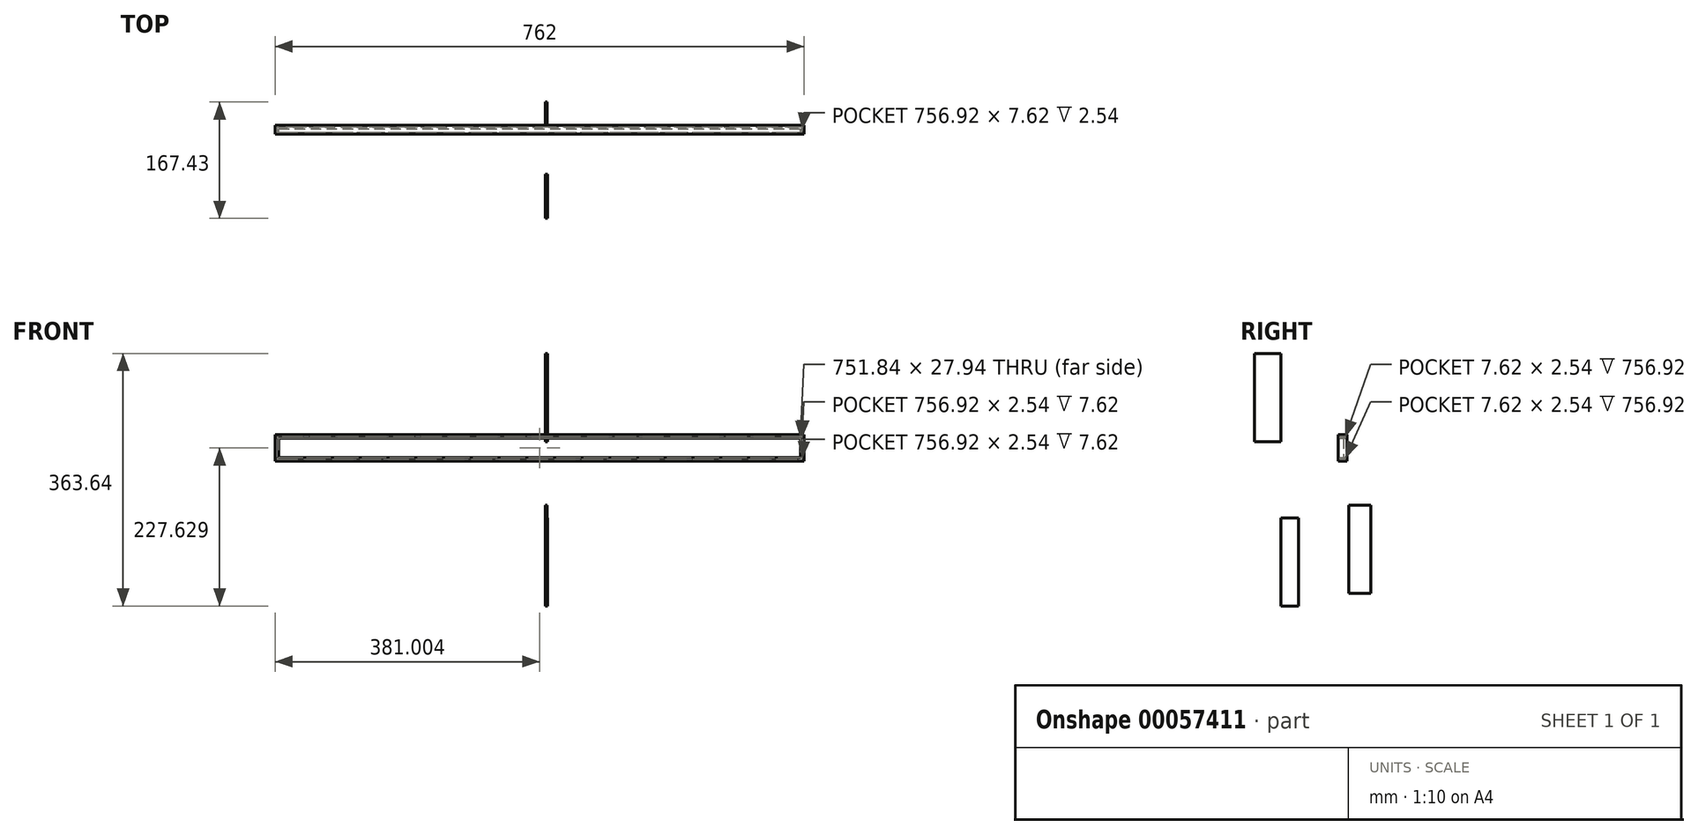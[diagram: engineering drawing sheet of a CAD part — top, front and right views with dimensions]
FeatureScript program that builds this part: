
annotation { "Feature Type Name" : "Feature", "Feature Type Description" : "" }
export const myFeature = defineFeature(function(context is Context, id is Id, definition is map)
    precondition{}
    {
        {
            var Q0;
            Q0=qCreatedBy(makeId("Front.planeOp"),FACE);
            var sketch = newSketch(context, id + "F0", { "sketchPlane" : qUnion([Q0])});
            skLineSegment(sketch, "E0.bottom", {"start": v(-388.9, 51.3) * mm, "end": v(373.1, 51.3) * mm});
            skLineSegment(sketch, "E0.top", {"start": v(-388.9, 13.2) * mm, "end": v(373.1, 13.2) * mm});
            skLineSegment(sketch, "E0.left", {"start": v(-388.9, 51.3) * mm, "end": v(-388.9, 13.2) * mm});
            skLineSegment(sketch, "E0.right", {"start": v(373.1, 51.3) * mm, "end": v(373.1, 13.2) * mm});
            skSolve(sketch);
        }
        {
            var Q0;
            Q0=makeQuery(id+"F0.imprint","IMPRINT",FACE,{"disambiguationData":[TD([[makeQuery(id+"F0.imprint","IMPRINT",EDGE,{"derivedFrom":sQuery(id+"F0.wireOp",EDGE,"E0.bottom")}),-1.0]])]});
            extrude(context, id + "F1", {"entities" : qUnion([Q0]), "depth" : 12.7 * mm});
        }
        {
            var Q0;
            Q0=makeQuery(id+"F1.opExtrude","CAP_FACE",FACE,{"disambiguationData":[OSD([sQuery(id+"F0.wireOp",EDGE,"E0.bottom"),sQuery(id+"F0.wireOp",EDGE,"E0.top"),sQuery(id+"F0.wireOp",EDGE,"E0.left"),sQuery(id+"F0.wireOp",EDGE,"E0.right")])],"isStart":false});
            shell(context, id + "F2", {"entities" : qUnion([Q0]), "thickness" : 5.08 * mm});
        }
        {
            var Q0;
            Q0=makeQuery(id+"F2.opShell","OFFSET_FACE",FACE,{"disambiguationData":[OSD([sQuery(id+"F0.wireOp",EDGE,"E0.bottom")])]});
            var Q1;
            Q1=makeQuery(id+"F2.opShell","OFFSET_FACE",FACE,{"disambiguationData":[OSD([sQuery(id+"F0.wireOp",EDGE,"E0.top")])]});
            shell(context, id + "F3", {"entities" : qUnion([Q0, Q1]), "thickness" : 2.54 * mm});
        }
        {
            var Q0;
            Q0=qCreatedBy(makeId("Right.planeOp"),FACE);
            var sketch = newSketch(context, id + "F4", { "sketchPlane" : qUnion([Q0])});
            skLineSegment(sketch, "E1.bottom", {"start": v(-95.64, -195.38) * mm, "end": v(-70.24, -195.38) * mm});
            skLineSegment(sketch, "E1.top", {"start": v(-95.64, -68.38) * mm, "end": v(-70.24, -68.38) * mm});
            skLineSegment(sketch, "E1.left", {"start": v(-95.64, -195.38) * mm, "end": v(-95.64, -68.38) * mm});
            skLineSegment(sketch, "E1.right", {"start": v(-70.24, -195.38) * mm, "end": v(-70.24, -68.38) * mm});
            skLineSegment(sketch, "E2.bottom", {"start": v(2.05, -176.92) * mm, "end": v(33.8, -176.92) * mm});
            skLineSegment(sketch, "E2.top", {"start": v(2.05, -49.92) * mm, "end": v(33.8, -49.92) * mm});
            skLineSegment(sketch, "E2.left", {"start": v(2.05, -176.92) * mm, "end": v(2.05, -49.92) * mm});
            skLineSegment(sketch, "E2.right", {"start": v(33.8, -176.92) * mm, "end": v(33.8, -49.92) * mm});
            skLineSegment(sketch, "E3.bottom", {"start": v(-133.63, 168.26) * mm, "end": v(-95.53, 168.26) * mm});
            skLineSegment(sketch, "E3.top", {"start": v(-133.63, 41.26) * mm, "end": v(-95.53, 41.26) * mm});
            skLineSegment(sketch, "E3.left", {"start": v(-133.63, 168.26) * mm, "end": v(-133.63, 41.26) * mm});
            skLineSegment(sketch, "E3.right", {"start": v(-95.53, 168.26) * mm, "end": v(-95.53, 41.26) * mm});
            skSolve(sketch);
        }
        {
            var Q0;
            Q0=makeQuery(id+"F4.imprint","IMPRINT",FACE,{"disambiguationData":[TD([[makeQuery(id+"F4.imprint","IMPRINT",EDGE,{"derivedFrom":sQuery(id+"F4.wireOp",EDGE,"E3.bottom")}),-1.0]])]});
            extrude(context, id + "F5", {"entities" : qUnion([Q0]), "depth" : 3.17 * mm});
        }
        {
            var Q0;
            Q0=makeQuery(id+"F4.imprint","IMPRINT",FACE,{"disambiguationData":[TD([[makeQuery(id+"F4.imprint","IMPRINT",EDGE,{"derivedFrom":sQuery(id+"F4.wireOp",EDGE,"E1.bottom")}),1.0]])]});
            extrude(context, id + "F6", {"entities" : qUnion([Q0]), "depth" : 3.17 * mm});
        }
        {
            var Q0;
            Q0=makeQuery(id+"F4.imprint","IMPRINT",FACE,{"disambiguationData":[TD([[makeQuery(id+"F4.imprint","IMPRINT",EDGE,{"derivedFrom":sQuery(id+"F4.wireOp",EDGE,"E2.bottom")}),1.0]])]});
            extrude(context, id + "F7", {"entities" : qUnion([Q0]), "depth" : 2.54 * mm});
        }
    });
